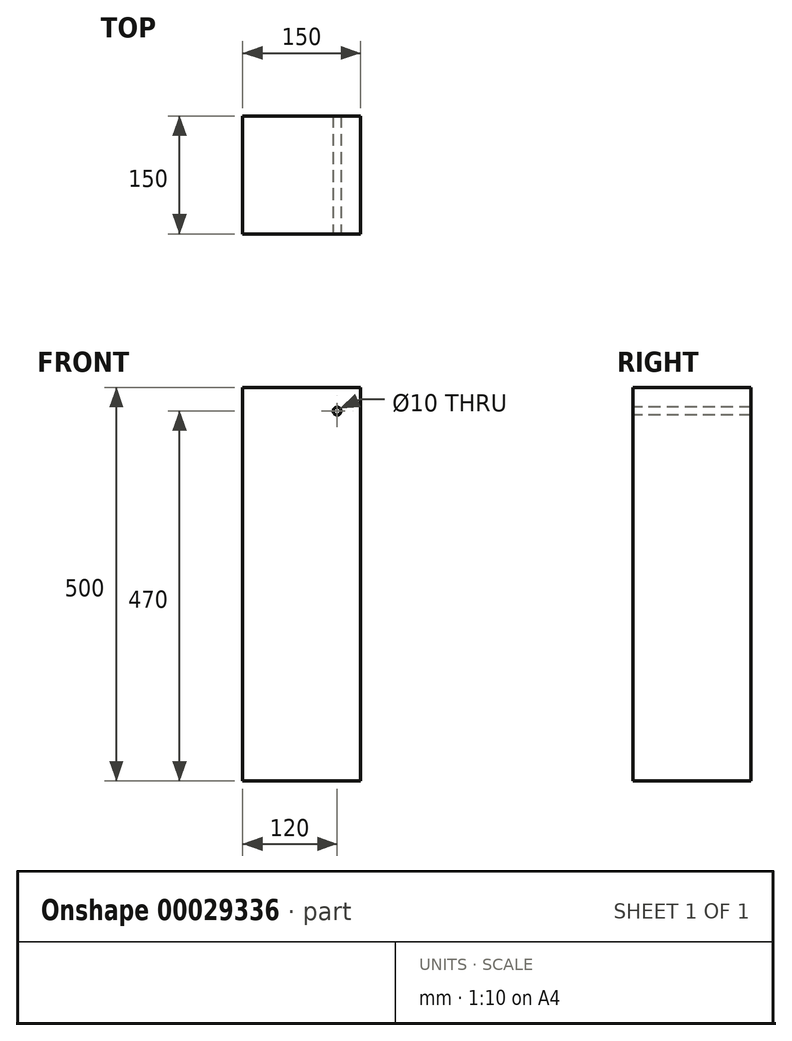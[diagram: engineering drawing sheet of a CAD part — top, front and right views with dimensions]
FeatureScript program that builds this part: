
annotation { "Feature Type Name" : "Feature", "Feature Type Description" : "" }
export const myFeature = defineFeature(function(context is Context, id is Id, definition is map)
    precondition{}
    {
        {
            var Q0;
            Q0=qCreatedBy(makeId("Front.planeOp"),FACE);
            var sketch = newSketch(context, id + "F0", { "sketchPlane" : qUnion([Q0])});
            skLineSegment(sketch, "E0.bottom", {"start": v(0, 0) * mm, "end": v(-150, 0) * mm});
            skLineSegment(sketch, "E0.top", {"start": v(0, 500) * mm, "end": v(-150, 500) * mm});
            skLineSegment(sketch, "E0.left", {"start": v(0, 0) * mm, "end": v(0, 500) * mm});
            skLineSegment(sketch, "E0.right", {"start": v(-150, 0) * mm, "end": v(-150, 500) * mm});
            skSolve(sketch);
        }
        {
            var Q0;
            Q0=makeQuery(id+"F0.imprint","IMPRINT",FACE,{"disambiguationData":[TD([[makeQuery(id+"F0.imprint","IMPRINT",EDGE,{"derivedFrom":sQuery(id+"F0.wireOp",EDGE,"E0.bottom")}),-1.0]])]});
            extrude(context, id + "F1", {"entities" : qUnion([Q0]), "oppositeDirection" : true, "depth" : 150 * mm});
        }
        {
            var Q0;
            Q0=makeQuery(id+"F1.opExtrude","CAP_FACE",FACE,{"disambiguationData":[OSD([sQuery(id+"F0.wireOp",EDGE,"E0.bottom"),sQuery(id+"F0.wireOp",EDGE,"E0.top"),sQuery(id+"F0.wireOp",EDGE,"E0.left"),sQuery(id+"F0.wireOp",EDGE,"E0.right")])],"isStart":true});
            var sketch = newSketch(context, id + "F2", { "sketchPlane" : qUnion([Q0])});
            skPoint(sketch, "E1", {"position": v(-30, 470) * mm});
            skSolve(sketch);
        }
        {
            var Q0;
            Q0=sQuery(id+"F2.wireOp",VERTEX,"E1");
            var Q1;
            Q1=makeQuery(id+"F1.opExtrude","SWEPT_BODY",BODY,{"disambiguationData":[OSD([sQuery(id+"F0.wireOp",EDGE,"E0.bottom"),sQuery(id+"F0.wireOp",EDGE,"E0.top"),sQuery(id+"F0.wireOp",EDGE,"E0.left"),sQuery(id+"F0.wireOp",EDGE,"E0.right")])]});
            hole(context, id + "F3", {"style" : HoleStyle.SIMPLE, "holeDiameter" : 10 * mm, "endStyle" : HoleEndStyle.THROUGH, "locations" : qUnion([Q0]), "scope" : qUnion([Q1])});
        }
    });
